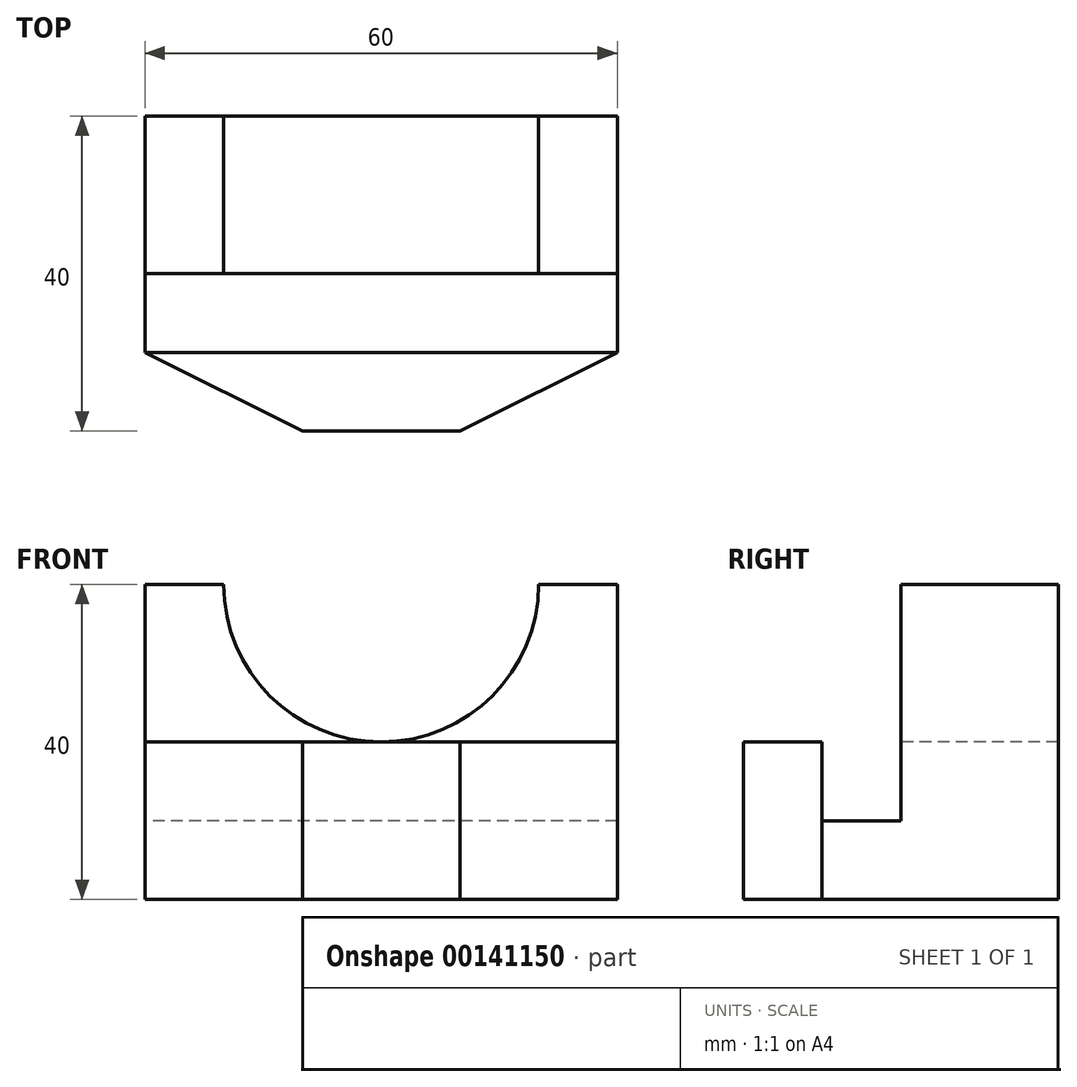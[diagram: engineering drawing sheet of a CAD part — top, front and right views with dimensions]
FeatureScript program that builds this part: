
annotation { "Feature Type Name" : "Feature", "Feature Type Description" : "" }
export const myFeature = defineFeature(function(context is Context, id is Id, definition is map)
    precondition{}
    {
        {
            var Q0;
            Q0=qCreatedBy(makeId("Front.planeOp"),FACE);
            var sketch = newSketch(context, id + "F0", { "sketchPlane" : qUnion([Q0])});
            skLineSegment(sketch, "E0", {"start": v(0, 0) * mm, "end": v(-60, 0) * mm});
            skLineSegment(sketch, "E1", {"start": v(-60, 0) * mm, "end": v(-60, 40) * mm});
            skLineSegment(sketch, "E2", {"start": v(-60, 40) * mm, "end": v(-50, 40) * mm});
            skLineSegment(sketch, "E3", {"start": v(0, 40) * mm, "end": v(0, 0) * mm});
            skPoint(sketch, "E4", {"position": v(-30, 40) * mm});
            skArc(sketch, "E5", {"start": v(-10, 40) * mm, "mid": v(-30, 20) * mm, "end": v(-50, 40) * mm});
            skPoint(sketch, "E6", {"position": v(-50, 40) * mm});
            skPoint(sketch, "E7", {"position": v(-10, 40) * mm});
            skLineSegment(sketch, "E8.trimOffspring", {"start": v(-10, 40) * mm, "end": v(0, 40) * mm});
            skSolve(sketch);
        }
        {
            var Q0;
            Q0 = qSketchRegion(id + "F0", true);
            extrude(context, id + "F1", {"entities" : qUnion([Q0]), "oppositeDirection" : true, "depth" : 20 * mm});
        }
        {
            var Q0;
            Q0=makeQuery(id+"F1.opExtrude","CAP_FACE",FACE,{"disambiguationData":[OSD([sQuery(id+"F0.wireOp",EDGE,"E0"),sQuery(id+"F0.wireOp",EDGE,"E1"),sQuery(id+"F0.wireOp",EDGE,"E2"),sQuery(id+"F0.wireOp",EDGE,"E3"),sQuery(id+"F0.wireOp",EDGE,"E5"),sQuery(id+"F0.wireOp",EDGE,"E8.trimOffspring")])],"isStart":true});
            var sketch = newSketch(context, id + "F2", { "sketchPlane" : qUnion([Q0])});
            skLineSegment(sketch, "E9", {"start": v(-60, 0) * mm, "end": v(0, 0) * mm});
            skLineSegment(sketch, "E10", {"start": v(0, 0) * mm, "end": v(0, 10) * mm});
            skLineSegment(sketch, "E11", {"start": v(0, 10) * mm, "end": v(-60, 10) * mm});
            skLineSegment(sketch, "E12", {"start": v(-60, 10) * mm, "end": v(-60, 0) * mm});
            skSolve(sketch);
        }
        {
            var Q0;
            Q0 = qSketchRegion(id + "F2", true);
            extrude(context, id + "F3", {"entities" : qUnion([Q0]), "operationType" : NewBodyOperationType.ADD, "depth" : 10 * mm});
        }
        {
            var Q0;
            Q0=makeQuery(id+"F3.boolean.opBoolean","MERGE",FACE,{"derivedFrom":[makeQuery(id+"F1.opExtrude","SWEPT_FACE",FACE,{"disambiguationData":[OSD([sQuery(id+"F0.wireOp",EDGE,"E0")])]}),makeQuery(id+"F3.opExtrude","SWEPT_FACE",FACE,{"disambiguationData":[OSD([sQuery(id+"F2.wireOp",EDGE,"E9")])]})]});
            var sketch = newSketch(context, id + "F4", { "sketchPlane" : qUnion([Q0])});
            skLineSegment(sketch, "E13", {"start": v(-60, 10) * mm, "end": v(0, 10) * mm});
            skLineSegment(sketch, "E14", {"start": v(0, 10) * mm, "end": v(-20, 20) * mm});
            skLineSegment(sketch, "E15", {"start": v(-20, 20) * mm, "end": v(-40, 20) * mm});
            skLineSegment(sketch, "E16", {"start": v(-40, 20) * mm, "end": v(-60, 10) * mm});
            skSolve(sketch);
        }
        {
            var Q0;
            Q0 = qSketchRegion(id + "F4", true);
            extrude(context, id + "F5", {"entities" : qUnion([Q0]), "operationType" : NewBodyOperationType.ADD, "oppositeDirection" : true, "depth" : 20 * mm});
        }
    });
